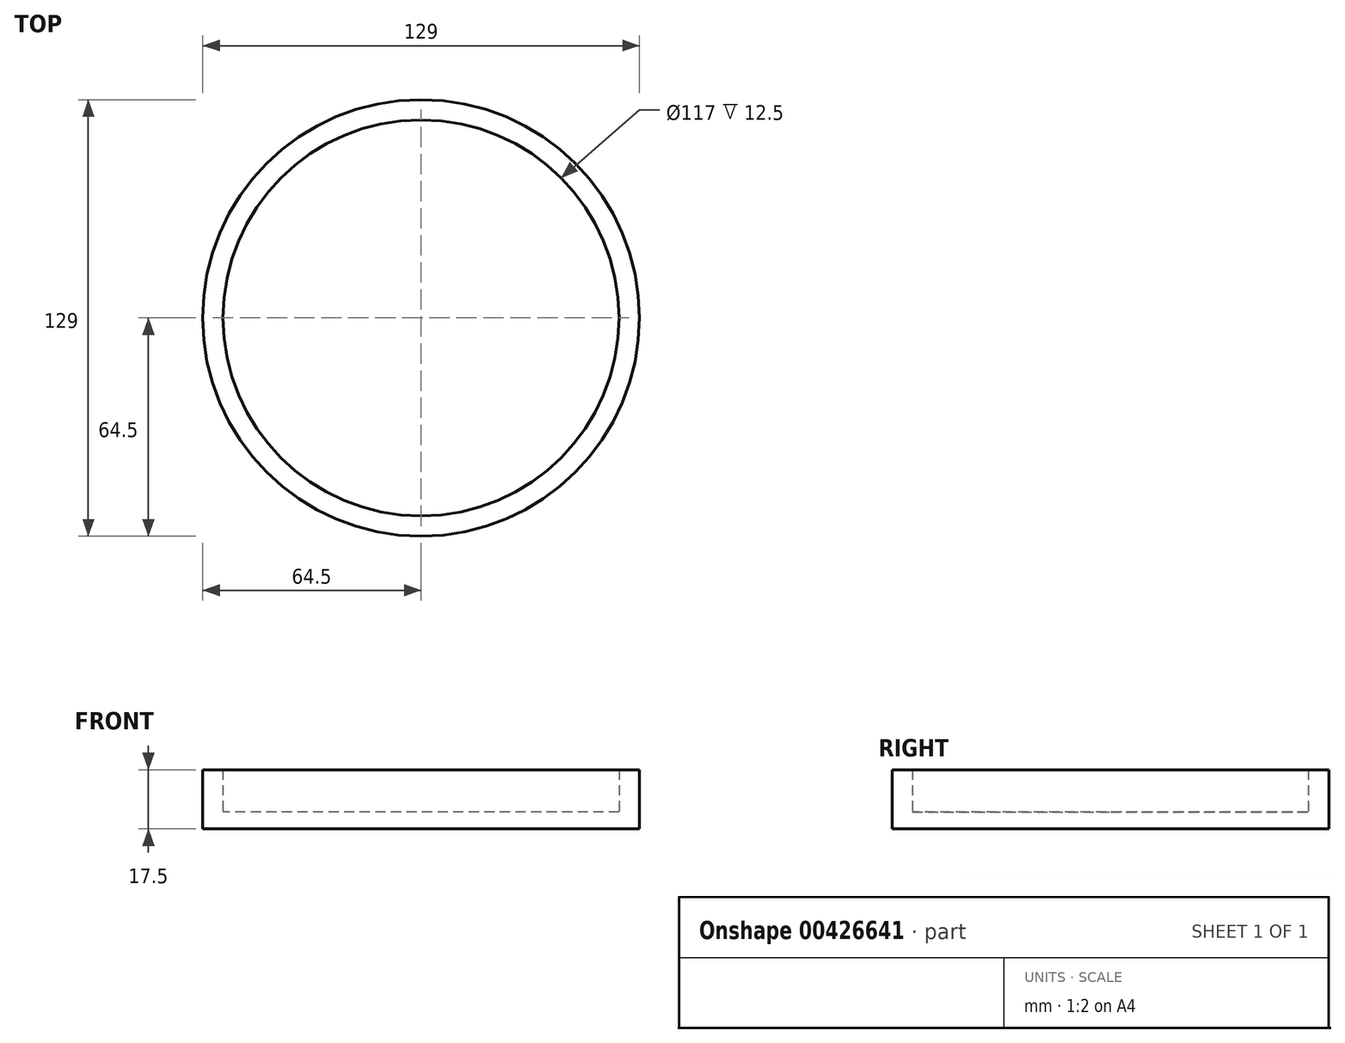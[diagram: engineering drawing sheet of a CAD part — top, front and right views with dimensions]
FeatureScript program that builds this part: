
annotation { "Feature Type Name" : "Feature", "Feature Type Description" : "" }
export const myFeature = defineFeature(function(context is Context, id is Id, definition is map)
    precondition{}
    {
        {
            var Q0;
            Q0=qCreatedBy(makeId("Top.planeOp"),FACE);
            var sketch = newSketch(context, id + "F0", { "sketchPlane" : qUnion([Q0])});
            skCircle(sketch, "E0", {"center": v(0, 0) * mm, "radius": 64.5 * mm});
            skCircle(sketch, "E1.0", {"center": v(0, 0) * mm, "radius": 58.5 * mm});
            skSolve(sketch);
        }
        {
            var Q0;
            Q0=makeQuery(id+"F0.imprint","IMPRINT",FACE,{"disambiguationData":[TD([[makeQuery(id+"F0.imprint","IMPRINT",EDGE,{"derivedFrom":sQuery(id+"F0.wireOp",EDGE,"E0")}),1.0]])]});
            var Q1;
            Q1=makeQuery(id+"F0.imprint","IMPRINT",FACE,{"disambiguationData":[TD([[makeQuery(id+"F0.imprint","IMPRINT",EDGE,{"derivedFrom":sQuery(id+"F0.wireOp",EDGE,"E1.0")}),1.0]])]});
            extrude(context, id + "F1", {"entities" : qUnion([Q0, Q1]), "depth" : 5 * mm});
        }
        {
            var Q0;
            Q0=qCreatedBy(makeId("Top.planeOp"),FACE);
            var sketch = newSketch(context, id + "F2", { "sketchPlane" : qUnion([Q0])});
            skCircle(sketch, "E2.0", {"center": v(0, 0) * mm, "radius": 64.5 * mm});
            skCircle(sketch, "E2.1", {"center": v(0, 0) * mm, "radius": 58.5 * mm});
            skSolve(sketch);
        }
        {
            var Q0;
            Q0 = qSketchRegion(id + "F2", true);
            extrude(context, id + "F3", {"entities" : qUnion([Q0]), "operationType" : NewBodyOperationType.ADD, "depth" : 17.5 * mm});
        }
    });
